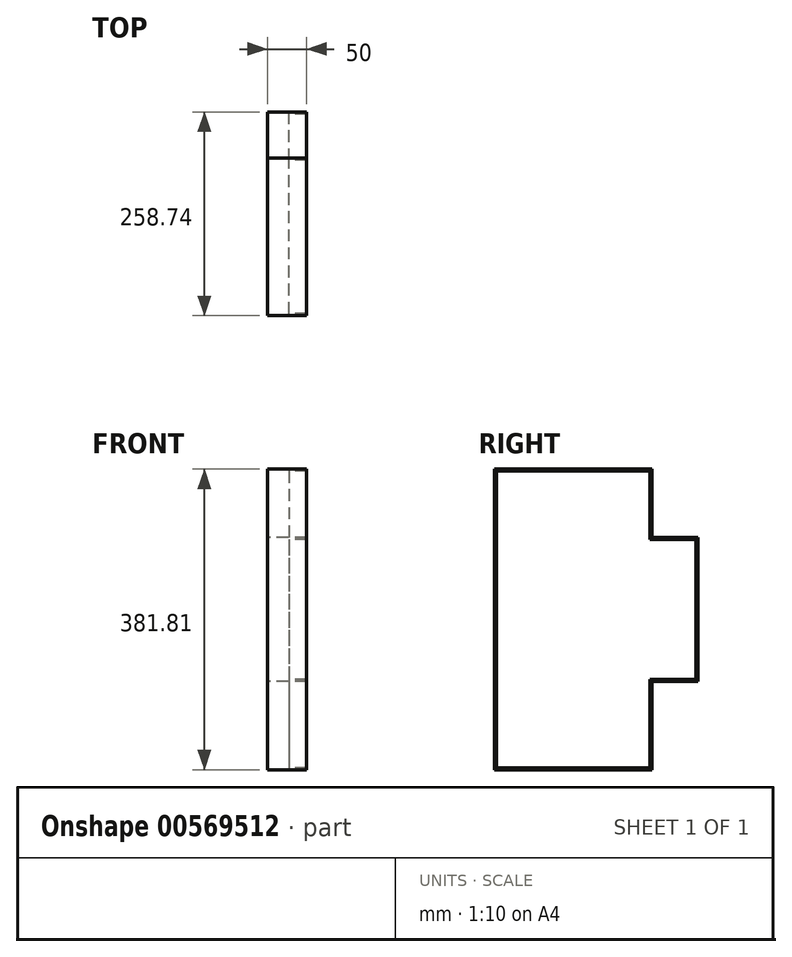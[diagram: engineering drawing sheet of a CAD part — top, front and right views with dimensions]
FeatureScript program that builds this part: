
annotation { "Feature Type Name" : "Feature", "Feature Type Description" : "" }
export const myFeature = defineFeature(function(context is Context, id is Id, definition is map)
    precondition{}
    {
        {
            var Q0;
            Q0=qCreatedBy(makeId("Right.planeOp"),FACE);
            var sketch = newSketch(context, id + "F0", { "sketchPlane" : qUnion([Q0])});
            skLineSegment(sketch, "E0.bottom", {"start": v(0, 89.46) * mm, "end": v(170.63, 89.46) * mm});
            skLineSegment(sketch, "E0.top", {"start": v(0, -93.39) * mm, "end": v(170.63, -93.39) * mm});
            skLineSegment(sketch, "E0.left", {"start": v(0, 89.46) * mm, "end": v(0, -93.39) * mm});
            skLineSegment(sketch, "E0.right", {"start": v(170.63, 89.46) * mm, "end": v(170.63, -93.39) * mm});
            skLineSegment(sketch, "E1.bottom", {"start": v(-88.11, 176.48) * mm, "end": v(111.89, 176.48) * mm});
            skLineSegment(sketch, "E1.top", {"start": v(-88.11, -205.33) * mm, "end": v(111.89, -205.33) * mm});
            skLineSegment(sketch, "E1.left", {"start": v(-88.11, 176.48) * mm, "end": v(-88.11, -205.33) * mm});
            skLineSegment(sketch, "E1.right", {"start": v(111.89, 176.48) * mm, "end": v(111.89, -205.33) * mm});
            skSolve(sketch);
        }
        {
            var Q0;
            Q0 = qSketchRegion(id + "F0", true);
            extrude(context, id + "F1", {"entities" : qUnion([Q0]), "depth" : 50 * mm, "offsetDistance" : 25.4 * mm});
        }
        {
            var Q0;
            Q0=makeQuery(id+"F1.opExtrude","CAP_FACE",FACE,{"disambiguationData":[OSD([sQuery(id+"F0.wireOp",EDGE,"E0.bottom"),sQuery(id+"F0.wireOp",EDGE,"E0.top"),sQuery(id+"F0.wireOp",EDGE,"E0.right"),sQuery(id+"F0.wireOp",EDGE,"E1.bottom"),sQuery(id+"F0.wireOp",EDGE,"E1.top"),sQuery(id+"F0.wireOp",EDGE,"E1.left"),sQuery(id+"F0.wireOp",EDGE,"E1.right")])],"isStart":false});
            shell(context, id + "F2", {"entities" : qUnion([Q0]), "thickness" : 2.54 * mm});
        }
        {
            var Q0;
            Q0=makeQuery(id+"F2.opShell","OFFSET_FACE",FACE,{"disambiguationData":[OSD([sQuery(id+"F0.wireOp",EDGE,"E0.bottom"),sQuery(id+"F0.wireOp",EDGE,"E0.top"),sQuery(id+"F0.wireOp",EDGE,"E0.right"),sQuery(id+"F0.wireOp",EDGE,"E1.bottom"),sQuery(id+"F0.wireOp",EDGE,"E1.top"),sQuery(id+"F0.wireOp",EDGE,"E1.left"),sQuery(id+"F0.wireOp",EDGE,"E1.right")])]});
            extrude(context, id + "F3", {"entities" : qUnion([Q0]), "operationType" : NewBodyOperationType.ADD, "depth" : 25 * mm, "offsetDistance" : 25 * mm});
        }
        {
            var Q0;
            Q0=makeQuery(id+"F3.opExtrude","CAP_FACE",FACE,{"disambiguationData":[OSD([sQuery(id+"F0.wireOp",EDGE,"E0.bottom"),sQuery(id+"F0.wireOp",EDGE,"E0.top"),sQuery(id+"F0.wireOp",EDGE,"E0.right"),sQuery(id+"F0.wireOp",EDGE,"E1.bottom"),sQuery(id+"F0.wireOp",EDGE,"E1.top"),sQuery(id+"F0.wireOp",EDGE,"E1.left"),sQuery(id+"F0.wireOp",EDGE,"E1.right")])],"isStart":false});
            var sketch = newSketch(context, id + "F4", { "sketchPlane" : qUnion([Q0])});
            skCircle(sketch, "E2", {"center": v(0, 0) * mm, "radius": 48.74 * mm});
            skSolve(sketch);
        }
        {
            var Q0;
            Q0 = qSketchRegion(id + "F4", true);
            extrude(context, id + "F5", {"entities" : qUnion([Q0]), "operationType" : NewBodyOperationType.ADD, "depth" : 25 * mm, "offsetDistance" : 25 * mm});
        }
        {
            var Q0;
            Q0=makeQuery(id+"F5.opExtrude","CAP_FACE",FACE,{"disambiguationData":[OSD([sQuery(id+"F4.wireOp",EDGE,"E2")])],"isStart":false});
            extrude(context, id + "F6", {"entities" : qUnion([Q0]), "operationType" : NewBodyOperationType.REMOVE, "oppositeDirection" : true, "depth" : 25 * mm, "offsetDistance" : 25 * mm});
        }
    });
